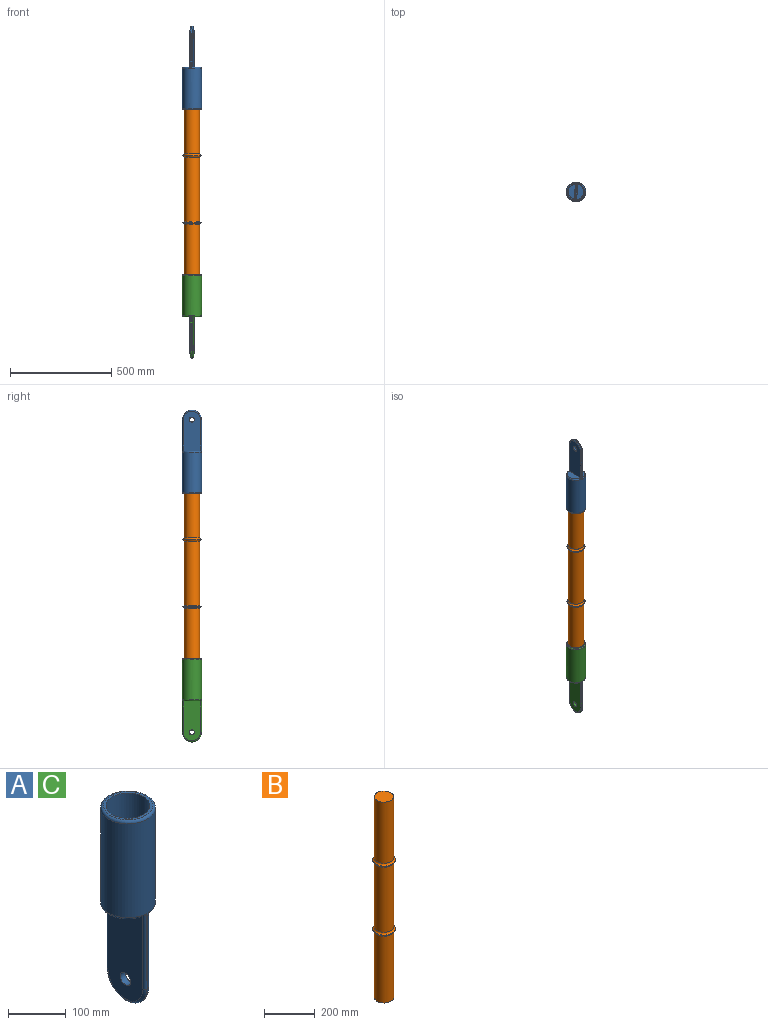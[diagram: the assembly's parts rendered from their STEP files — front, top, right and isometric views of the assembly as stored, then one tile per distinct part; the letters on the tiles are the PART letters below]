
ASSEMBLY  parts=3 mates=6
PART A: 25 faces, bbox 103.1x103.1x416.7 mm
  f0: plane 84.14x36.2mm, normal (0,0,-1), area 2305mm2, adj f15,f23
  f1: cylinder r=38.1mm len=203.2mm, axis (0,0,-1), area 48643.9mm2, adj f3,f4
  f2: cylinder r=47.62mm len=204.47mm, axis (0,0,-1), area 59703.1mm2, adj f6,f7,f8,f10,f16,f18,f19,f21
  f3: plane 85.09x85.09mm, normal (0,0,1), area 1126.2mm2, adj f1,f24
  f4: plane 76.2x76.2mm, normal (0,0,1), area 4560.4mm2, adj f1
  f5: plane 84.14x36.2mm, normal (0,0,-1), area 2305mm2, adj f14,f22
  f6: plane 1.88x0.04mm, normal (0,0,1), area 0mm2, adj f2,f9,f19
  f7: plane 1.88x0.04mm, normal (0,0,1), area 0mm2, adj f2,f9,f16
  f8: plane 1.88x0.04mm, normal (0,0,1), area 0mm2, adj f2,f11,f18
  f9: plane 155.58x2.54mm, normal (0,1,0), area 395.2mm2, adj f6,f7,f13,f16,f19
  f10: plane 1.88x0.04mm, normal (0,0,1), area 0mm2, adj f2,f11,f21
  f11: plane 155.58x2.54mm, normal (0,-1,0), area 395.2mm2, adj f8,f10,f13,f18,f21
  f12: cylinder r=12.7mm len=25.4mm, axis (-1,0,0), area 1013.4mm2, adj f14,f15
  f13: cylinder r=47.62mm len=95.25mm, axis (-1,0,0), area 380mm2, adj f9,f11,f17,f20
  f14: plane 198.14x85.09mm, normal (1,0,0), area 15574.4mm2, adj f5,f12,f19,f20,f21,f22
  f15: plane 198.14x85.09mm, normal (-1,0,0), area 15574.4mm2, adj f0,f12,f16,f17,f18,f23
  f16: cylinder r=5.08mm len=160.66mm, axis (0,0,1), area 1254.9mm2, adj f2,f7,f9,f15,f17,f23
  f17: torus R=42.55mm, axis (1,0,0), area 1147.6mm2, adj f13,f15,f16,f18
  f18: cylinder r=5.08mm len=160.66mm, axis (0,0,-1), area 1254.9mm2, adj f2,f8,f11,f15,f17,f23
  f19: cylinder r=5.08mm len=160.66mm, axis (0,0,-1), area 1254.9mm2, adj f2,f6,f9,f14,f20,f22
  f20: torus R=42.55mm, axis (1,0,0), area 1147.6mm2, adj f13,f14,f19,f21
  f21: cylinder r=5.08mm len=160.66mm, axis (0,0,1), area 1254.9mm2, adj f2,f10,f11,f14,f20,f22
  f22: torus R=42.55mm, axis (0,0,-1), area 1072mm2, adj f2,f5,f14,f19,f21
  f23: torus R=42.55mm, axis (0,0,-1), area 1072mm2, adj f0,f2,f15,f16,f18
  f24: torus R=42.55mm, axis (0,0,1), area 2295.3mm2, adj f2,f3
PART B: 11 faces, bbox 103.1x103.1x969.3 mm
  f0: plane 76.2x76.2mm, normal (0,0,1), area 4560.4mm2, adj f1
  f1: cylinder r=38.1mm len=295.28mm, axis (0,0,1), area 70685.7mm2, adj f0,f2
  f2: torus R=47.62mm, axis (0,0,1), area 2929.7mm2, adj f1,f3
  f3: torus R=44.09mm, axis (0,0,1), area 432.3mm2, adj f2,f4
  f4: torus R=47.62mm, axis (0,0,1), area 2929.7mm2, adj f3,f5
  f5: cylinder r=38.1mm len=313.89mm, axis (0,0,1), area 75142.9mm2, adj f4,f6
  f6: torus R=47.62mm, axis (0,0,1), area 2929.7mm2, adj f5,f7
  f7: torus R=44.09mm, axis (0,0,1), area 432.3mm2, adj f6,f8
  f8: torus R=47.62mm, axis (0,0,1), area 2929.7mm2, adj f7,f9
  f9: cylinder r=38.1mm len=322.01mm, axis (0,0,1), area 77084.7mm2, adj f8,f10
  f10: plane 76.2x76.2mm, normal (0,0,-1), area 4560.4mm2, adj f9
PART C: same geometry as A
PLACE A rot(axis=(1,-0.06,0),180deg) t=(351.36,24.77,863.92)mm
PLACE B rot(axis=(0,0,-1),6.3deg) t=(351.36,24.77,265.65)mm
PLACE C rot(axis=(0,0,-1),6.3deg) t=(351.36,24.77,-359.35)mm
MATE cylindrical A.f1 <-> B.f1  axis (0,0,1) through (351.36,24.77,660.72)mm
MATE planar B.f1 <-> A.f1  axis (0,0,1) through (351.36,24.77,736.92)mm
MATE parallel B.f1 <-> A.f1  axis (0,0,1) through (351.36,24.77,736.92)mm
MATE fastened B.f1 <-> C.f1  axis (0,0,-1) through (351.36,24.77,-232.35)mm
MATE parallel A.f14 <-> C.f14  axis (0.99,-0.11,0) through (357.67,24.07,963.03)mm
MATE cylindrical B.f1 <-> C.f1  axis (0,0,1) through (351.36,24.77,-232.35)mm
